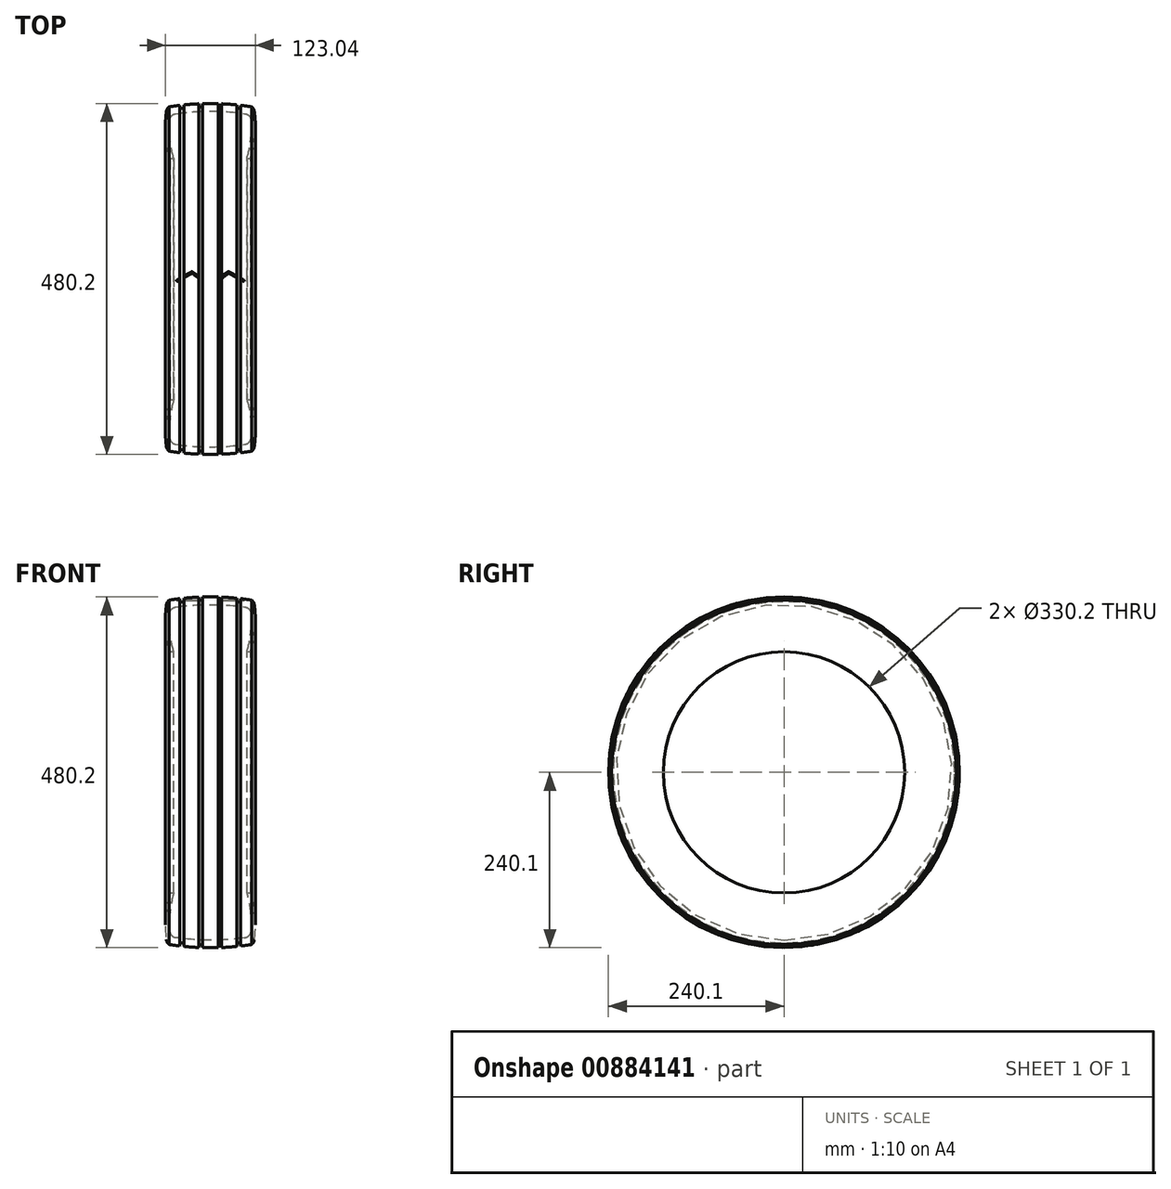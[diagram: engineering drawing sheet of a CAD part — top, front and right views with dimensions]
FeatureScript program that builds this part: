
annotation { "Feature Type Name" : "Feature", "Feature Type Description" : "" }
export const myFeature = defineFeature(function(context is Context, id is Id, definition is map)
    precondition{}
    {
        {
            var Q0;
            Q0=qCreatedBy(makeId("Top.planeOp"),FACE);
            var sketch = newSketch(context, id + "F0", { "sketchPlane" : qUnion([Q0])});
            skLineSegment(sketch, "E0", {"start": v(0, 165.1) * mm, "end": v(0, 240.1) * mm, "construction": true});
            skLineSegment(sketch, "E1", {"start": v(0, 165.1) * mm, "end": v(-55, 165.1) * mm, "construction": true});
            skLineSegment(sketch, "E2", {"start": v(0, 230.1) * mm, "end": v(-60, 230.1) * mm, "construction": true});
            skArc(sketch, "E3", {"start": v(-60.1, 229.37) * mm, "mid": v(-61.05, 196.96) * mm, "end": v(-55, 165.1) * mm});
            skPoint(sketch, "E4.visualSharp", {"position": v(-60, 230.1) * mm});
            skArc(sketch, "E4.filletArc", {"start": v(-56.66, 235.63) * mm, "mid": v(-58.96, 232.82) * mm, "end": v(-60.1, 229.37) * mm});
            skArc(sketch, "E5.MirrorCS", {"start": v(56.66, 235.63) * mm, "mid": v(58.96, 232.82) * mm, "end": v(60.1, 229.37) * mm});
            skArc(sketch, "E6.MirrorCS", {"start": v(60.1, 229.37) * mm, "mid": v(61.05, 196.96) * mm, "end": v(55, 165.1) * mm});
            skLineSegment(sketch, "E7", {"start": v(0, 165.1) * mm, "end": v(0, 0) * mm, "construction": true});
            skLineSegment(sketch, "E8", {"start": v(0, 0) * mm, "end": v(-59.26, 0) * mm, "construction": true});
            skArc(sketch, "E9", {"start": v(56.66, 235.63) * mm, "mid": v(0, 240.1) * mm, "end": v(-56.66, 235.63) * mm});
            skLineSegment(sketch, "E10", {"start": v(-55, 165.1) * mm, "end": v(-50, 165.1) * mm});
            skLineSegment(sketch, "E11", {"start": v(0, 225.1) * mm, "end": v(-55, 225.1) * mm, "construction": true});
            skArc(sketch, "E12", {"start": v(-55.78, 217.12) * mm, "mid": v(-55.25, 190.85) * mm, "end": v(-50, 165.1) * mm});
            skArc(sketch, "E13.MirrorCS", {"start": v(55.78, 217.12) * mm, "mid": v(55.25, 190.85) * mm, "end": v(50, 165.1) * mm});
            skLineSegment(sketch, "E14.MirrorCS", {"start": v(55, 165.1) * mm, "end": v(50, 165.1) * mm});
            skArc(sketch, "E15", {"start": v(47.24, 226.32) * mm, "mid": v(0, 229.73) * mm, "end": v(-47.24, 226.32) * mm});
            skPoint(sketch, "E16.visualSharp", {"position": v(-55, 225.1) * mm});
            skArc(sketch, "E16.filletArc", {"start": v(-47.24, 226.32) * mm, "mid": v(-53.13, 223.23) * mm, "end": v(-55.78, 217.12) * mm});
            skPoint(sketch, "E17.visualSharp", {"position": v(55, 225.1) * mm});
            skArc(sketch, "E17.filletArc", {"start": v(55.78, 217.12) * mm, "mid": v(53.13, 223.23) * mm, "end": v(47.24, 226.32) * mm});
            skSolve(sketch);
        }
        {
            var Q0;
            Q0 = qSketchRegion(id + "F0", true);
            var Q1;
            Q1=sQuery(id+"F0.wireOp",EDGE,"E8");
            revolve(context, id + "F1", {"surfaceOperationType" : NewSurfaceOperationType.NEW, "entities" : qUnion([Q0]), "axis" : qUnion([Q1]), "revolveType" : RevolveType.FULL});
        }
        {
            var Q0;
            Q0=qCreatedBy(makeId("Top.planeOp"),FACE);
            var sketch = newSketch(context, id + "F2", { "sketchPlane" : qUnion([Q0])});
            skLineSegment(sketch, "E18", {"start": v(0, 0) * mm, "end": v(270.8, 0) * mm, "construction": true});
            skLineSegment(sketch, "E19.bottom", {"start": v(-41.6, 241.96) * mm, "end": v(-36.4, 241.96) * mm});
            skLineSegment(sketch, "E19.top", {"start": v(-41.6, 233.5) * mm, "end": v(-36.4, 233.5) * mm});
            skLineSegment(sketch, "E19.left", {"start": v(-41.6, 241.96) * mm, "end": v(-41.6, 233.5) * mm});
            skLineSegment(sketch, "E19.right", {"start": v(-36.4, 241.96) * mm, "end": v(-36.4, 233.5) * mm});
            skLineSegment(sketch, "E20", {"start": v(0, 0) * mm, "end": v(0, 233.5) * mm, "construction": true});
            skLineSegment(sketch, "E21", {"start": v(0, 233.5) * mm, "end": v(-36.4, 233.5) * mm, "construction": true});
            skLineSegment(sketch, "E22.MirrorCS", {"start": v(36.4, 241.96) * mm, "end": v(36.4, 233.5) * mm});
            skLineSegment(sketch, "E23.MirrorCS", {"start": v(41.6, 241.96) * mm, "end": v(36.4, 241.96) * mm});
            skLineSegment(sketch, "E24.MirrorCS", {"start": v(41.6, 241.96) * mm, "end": v(41.6, 233.5) * mm});
            skLineSegment(sketch, "E25.MirrorCS", {"start": v(41.6, 233.5) * mm, "end": v(36.4, 233.5) * mm});
            skLineSegment(sketch, "E26.bottom", {"start": v(-15.63, 242.6) * mm, "end": v(-10.86, 242.6) * mm});
            skLineSegment(sketch, "E26.top", {"start": v(-15.63, 235.88) * mm, "end": v(-10.86, 235.88) * mm});
            skLineSegment(sketch, "E26.left", {"start": v(-15.63, 242.6) * mm, "end": v(-15.63, 235.88) * mm});
            skLineSegment(sketch, "E26.right", {"start": v(-10.86, 242.6) * mm, "end": v(-10.86, 235.88) * mm});
            skLineSegment(sketch, "E27.MirrorCS", {"start": v(15.63, 242.6) * mm, "end": v(10.86, 242.6) * mm});
            skLineSegment(sketch, "E28.MirrorCS", {"start": v(10.86, 242.6) * mm, "end": v(10.86, 235.88) * mm});
            skLineSegment(sketch, "E29.MirrorCS", {"start": v(15.63, 242.6) * mm, "end": v(15.63, 235.88) * mm});
            skLineSegment(sketch, "E30.MirrorCS", {"start": v(15.63, 235.88) * mm, "end": v(10.86, 235.88) * mm});
            skSolve(sketch);
        }
        {
            var Q0;
            Q0 = qSketchRegion(id + "F2", true);
            var Q1;
            Q1=sQuery(id+"F2.wireOp",EDGE,"E18");
            revolve(context, id + "F3", {"operationType" : NewBodyOperationType.REMOVE, "surfaceOperationType" : NewSurfaceOperationType.NEW, "entities" : qUnion([Q0]), "axis" : qUnion([Q1]), "revolveType" : RevolveType.FULL, "oppositeDirection" : true});
        }
        {
            var Q0;
            Q0=qCreatedBy(makeId("Top.planeOp"),FACE);
            cPlane(context, id + "F4", {"entities" : qUnion([Q0]), "cplaneType" : CPlaneType.OFFSET, "offset" : 250 * mm, "width" : 150 * mm, "height" : 150 * mm});
        }
        {
            var Q0;
            Q0=qCreatedBy(id+"F4.planeOp",FACE);
            var sketch = newSketch(context, id + "F5", { "sketchPlane" : qUnion([Q0])});
            skLineSegment(sketch, "E31", {"start": v(0, 0) * mm, "end": v(0, -15.06) * mm, "construction": true});
            skLineSegment(sketch, "E32", {"start": v(0, 0) * mm, "end": v(10.62, 0) * mm, "construction": true});
            skLineSegment(sketch, "E33", {"start": v(10.62, 0) * mm, "end": v(25.25, 10.28) * mm});
            skLineSegment(sketch, "E34", {"start": v(25.25, 10.28) * mm, "end": v(46.44, -1.74) * mm});
            skLineSegment(sketch, "E35", {"start": v(46.44, -1.74) * mm, "end": v(45.49, -3.42) * mm});
            skLineSegment(sketch, "E36", {"start": v(45.49, -3.42) * mm, "end": v(25.5, 7.9) * mm});
            skLineSegment(sketch, "E37", {"start": v(25.5, 7.9) * mm, "end": v(15.6, 0.94) * mm});
            skLineSegment(sketch, "E38", {"start": v(15.6, 0.94) * mm, "end": v(15.6, 3.5) * mm});
            skLineSegment(sketch, "E39.MirrorCS", {"start": v(-10.62, 0) * mm, "end": v(-25.25, 10.28) * mm});
            skLineSegment(sketch, "E40.MirrorCS", {"start": v(-25.5, 7.9) * mm, "end": v(-15.6, 0.94) * mm});
            skLineSegment(sketch, "E41.MirrorCS", {"start": v(-15.6, 0.94) * mm, "end": v(-15.6, 3.5) * mm});
            skLineSegment(sketch, "E42.MirrorCS", {"start": v(-46.44, -1.74) * mm, "end": v(-45.49, -3.42) * mm});
            skLineSegment(sketch, "E43.MirrorCS", {"start": v(-25.25, 10.28) * mm, "end": v(-46.44, -1.74) * mm});
            skLineSegment(sketch, "E44.MirrorCS", {"start": v(-45.49, -3.42) * mm, "end": v(-25.5, 7.9) * mm});
            skSolve(sketch);
        }
        {
            var Q0;
            Q0 = qSketchRegion(id + "F5", true);
            extrude(context, id + "F6", {"entities" : qUnion([Q0]), "operationType" : NewBodyOperationType.REMOVE, "oppositeDirection" : true, "depth" : 15 * mm, "offsetDistance" : 25 * mm});
        }
    });
